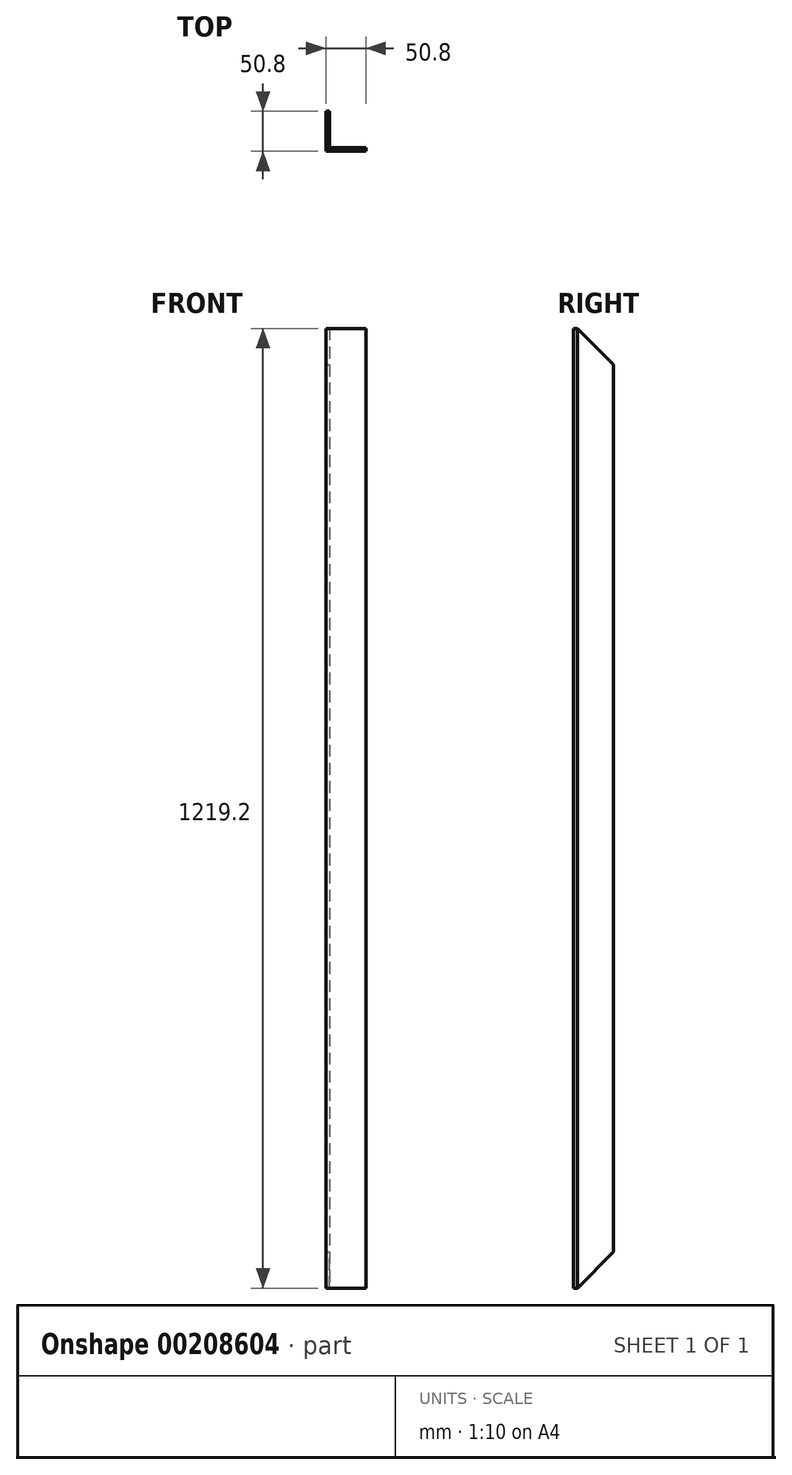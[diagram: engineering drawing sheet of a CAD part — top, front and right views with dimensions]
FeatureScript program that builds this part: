
annotation { "Feature Type Name" : "Feature", "Feature Type Description" : "" }
export const myFeature = defineFeature(function(context is Context, id is Id, definition is map)
    precondition{}
    {
        {
            var Q0;
            Q0=qCreatedBy(makeId("Top.planeOp"),FACE);
            var sketch = newSketch(context, id + "F0", { "sketchPlane" : qUnion([Q0])});
            skLineSegment(sketch, "E0", {"start": v(0, 0) * mm, "end": v(50.8, 0) * mm});
            skLineSegment(sketch, "E1", {"start": v(0, 0) * mm, "end": v(0, 50.8) * mm});
            skLineSegment(sketch, "E2.0", {"start": v(4.76, 4.76) * mm, "end": v(4.76, 50.8) * mm});
            skLineSegment(sketch, "E2.1", {"start": v(4.76, 4.76) * mm, "end": v(50.8, 4.76) * mm});
            skLineSegment(sketch, "E3", {"start": v(4.76, 50.8) * mm, "end": v(0, 50.8) * mm});
            skLineSegment(sketch, "E4", {"start": v(50.8, 4.76) * mm, "end": v(50.8, 0) * mm});
            skSolve(sketch);
        }
        {
            var Q0;
            Q0 = qSketchRegion(id + "F0", true);
            extrude(context, id + "F1", {"entities" : qUnion([Q0]), "depth" : 1219.2 * mm});
        }
        {
            var Q0;
            Q0=makeQuery(id+"F1.opExtrude","SWEPT_FACE",FACE,{"disambiguationData":[OSD([sQuery(id+"F0.wireOp",EDGE,"E2.0")])]});
            var sketch = newSketch(context, id + "F2", { "sketchPlane" : qUnion([Q0])});
            skLineSegment(sketch, "E5", {"start": v(4.76, 0) * mm, "end": v(50.8, 46.04) * mm});
            skLineSegment(sketch, "E6", {"start": v(50.8, 46.04) * mm, "end": v(50.8, 0) * mm});
            skLineSegment(sketch, "E7", {"start": v(50.8, 0) * mm, "end": v(4.76, 0) * mm});
            skLineSegment(sketch, "E8", {"start": v(4.76, 1219.2) * mm, "end": v(50.8, 1173.16) * mm});
            skLineSegment(sketch, "E9", {"start": v(50.8, 1173.16) * mm, "end": v(50.8, 1219.2) * mm});
            skLineSegment(sketch, "E10", {"start": v(50.8, 1219.2) * mm, "end": v(4.76, 1219.2) * mm});
            skSolve(sketch);
        }
        {
            var Q0;
            Q0 = qSketchRegion(id + "F2", true);
            var Q1;
            Q1=makeQuery(id+"F1.opExtrude","SWEPT_FACE",FACE,{"disambiguationData":[OSD([sQuery(id+"F0.wireOp",EDGE,"E1")])]});
            extrude(context, id + "F3", {"entities" : qUnion([Q0]), "operationType" : NewBodyOperationType.REMOVE, "endBound" : BoundingType.UP_TO_SURFACE, "oppositeDirection" : true, "endBoundEntityFace" : qUnion([Q1]), "depth" : 25.4 * mm});
        }
    });
